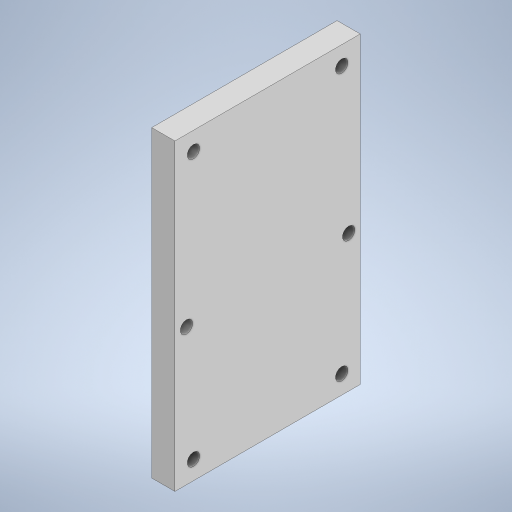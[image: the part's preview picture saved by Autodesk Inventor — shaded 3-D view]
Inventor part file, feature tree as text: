
AUTODESK INVENTOR PART (.ipt)
format: ipt  version: 2023 (Build 270158000, 158)  size: 250,368 bytes
history: native  units: in
note: dims shown in document units (in); Inventor stores cm internally (conversion verified against a paired STEP export)
features: extrude x1
ambient origin geometry x8: Origin, YZ Plane, XZ Plane, XY Plane, X Axis, Y Axis, Z Axis, Center Point
bodies: Solid1 (feature_tree)
feature tree (1):
  extrude  "Extrusion1"  Depth=3.275in
